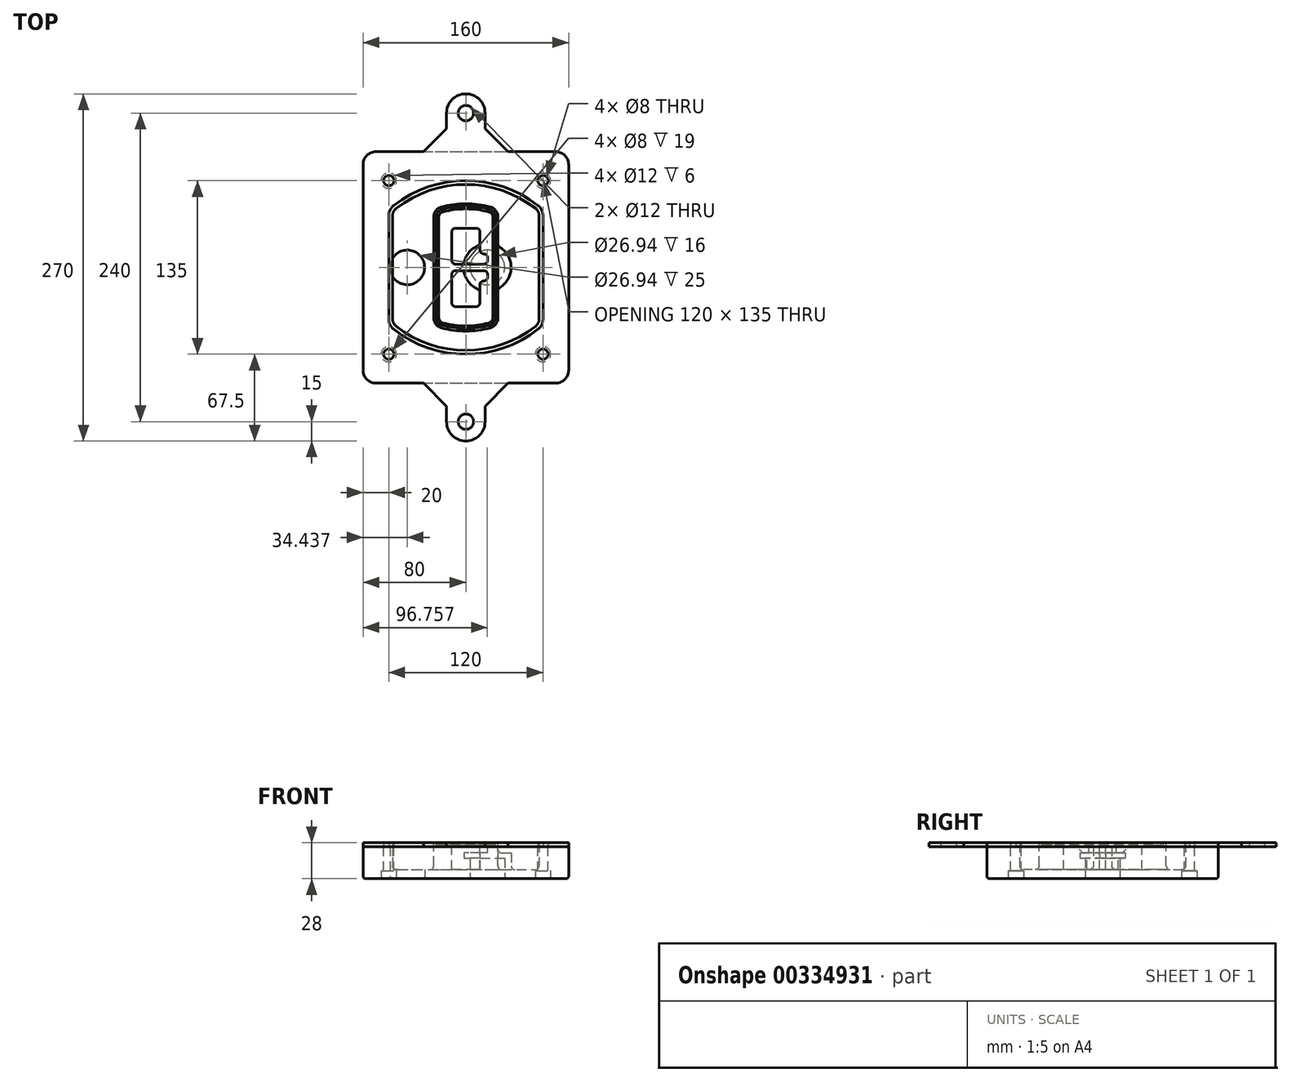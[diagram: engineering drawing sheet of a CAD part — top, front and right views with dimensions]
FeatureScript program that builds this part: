
annotation { "Feature Type Name" : "Feature", "Feature Type Description" : "" }
export const myFeature = defineFeature(function(context is Context, id is Id, definition is map)
    precondition{}
    {
        {
            var Q0;
            Q0=qCreatedBy(makeId("Top.planeOp"),FACE);
            var sketch = newSketch(context, id + "F0", { "sketchPlane" : qUnion([Q0])});
            skPoint(sketch, "E0.rect.middle", {"position": v(0, 0) * mm});
            skLineSegment(sketch, "E1.bottom", {"start": v(-70, -90) * mm, "end": v(70, -90) * mm});
            skLineSegment(sketch, "E1.top", {"start": v(-70, 90) * mm, "end": v(70, 90) * mm});
            skLineSegment(sketch, "E1.left", {"start": v(-80, -80) * mm, "end": v(-80, 80) * mm});
            skLineSegment(sketch, "E1.right", {"start": v(80, -80) * mm, "end": v(80, 80) * mm});
            skLineSegment(sketch, "E2", {"start": v(-80, 90) * mm, "end": v(80, -90) * mm, "construction": true});
            skLineSegment(sketch, "E3", {"start": v(80, 90) * mm, "end": v(-80, -90) * mm, "construction": true});
            skCircle(sketch, "E4", {"center": v(-60, 67.5) * mm, "radius": 4 * mm});
            skCircle(sketch, "E5", {"center": v(60, 67.5) * mm, "radius": 4 * mm});
            skCircle(sketch, "E6", {"center": v(60, -67.5) * mm, "radius": 4 * mm});
            skCircle(sketch, "E7", {"center": v(-60, -67.5) * mm, "radius": 4 * mm});
            skLineSegment(sketch, "E8", {"start": v(-60, 67.5) * mm, "end": v(60, 67.5) * mm, "construction": true});
            skLineSegment(sketch, "E9", {"start": v(60, 67.5) * mm, "end": v(60, -67.5) * mm, "construction": true});
            skLineSegment(sketch, "E10", {"start": v(60, -67.5) * mm, "end": v(-60, -67.5) * mm, "construction": true});
            skLineSegment(sketch, "E11", {"start": v(-60, -67.5) * mm, "end": v(-60, 67.5) * mm, "construction": true});
            skLineSegment(sketch, "E12", {"start": v(-60, 40.3) * mm, "end": v(-60, -40.3) * mm});
            skLineSegment(sketch, "E13", {"start": v(60, 40.3) * mm, "end": v(60, -40.3) * mm});
            skArc(sketch, "E14", {"start": v(56.15, 48.18) * mm, "mid": v(0, 67.5) * mm, "end": v(-56.15, 48.18) * mm});
            skArc(sketch, "E15", {"start": v(-56.15, -48.18) * mm, "mid": v(0, -67.5) * mm, "end": v(56.15, -48.18) * mm});
            skLineSegment(sketch, "E16", {"start": v(-60, 0) * mm, "end": v(60, 0) * mm, "construction": true});
            skPoint(sketch, "E17.visualSharp", {"position": v(-60, -45) * mm});
            skArc(sketch, "E17.filletArc", {"start": v(-60, -40.3) * mm, "mid": v(-58.99, -44.68) * mm, "end": v(-56.15, -48.18) * mm});
            skPoint(sketch, "E18.visualSharp", {"position": v(-60, 45) * mm});
            skArc(sketch, "E18.filletArc", {"start": v(-56.15, 48.18) * mm, "mid": v(-58.99, 44.68) * mm, "end": v(-60, 40.3) * mm});
            skPoint(sketch, "E19.visualSharp", {"position": v(60, 45) * mm});
            skArc(sketch, "E19.filletArc", {"start": v(60, 40.3) * mm, "mid": v(58.99, 44.68) * mm, "end": v(56.15, 48.18) * mm});
            skPoint(sketch, "E20.visualSharp", {"position": v(60, -45) * mm});
            skArc(sketch, "E20.filletArc", {"start": v(56.15, -48.18) * mm, "mid": v(58.99, -44.68) * mm, "end": v(60, -40.3) * mm});
            skPoint(sketch, "E21.visualSharp", {"position": v(-80, 90) * mm});
            skArc(sketch, "E21.filletArc", {"start": v(-70, 90) * mm, "mid": v(-77.07, 87.07) * mm, "end": v(-80, 80) * mm});
            skPoint(sketch, "E22.visualSharp", {"position": v(80, 90) * mm});
            skArc(sketch, "E22.filletArc", {"start": v(80, 80) * mm, "mid": v(77.07, 87.07) * mm, "end": v(70, 90) * mm});
            skPoint(sketch, "E23.visualSharp", {"position": v(80, -90) * mm});
            skArc(sketch, "E23.filletArc", {"start": v(70, -90) * mm, "mid": v(77.07, -87.07) * mm, "end": v(80, -80) * mm});
            skPoint(sketch, "E24.visualSharp", {"position": v(-80, -90) * mm});
            skArc(sketch, "E24.filletArc", {"start": v(-80, -80) * mm, "mid": v(-77.07, -87.07) * mm, "end": v(-70, -90) * mm});
            skArc(sketch, "E25.0", {"start": v(57, 40.3) * mm, "mid": v(56.3, 43.36) * mm, "end": v(54.3, 45.81) * mm});
            skLineSegment(sketch, "E25.1", {"start": v(57, 40.3) * mm, "end": v(57, -40.3) * mm});
            skArc(sketch, "E25.2", {"start": v(54.3, -45.81) * mm, "mid": v(56.3, -43.36) * mm, "end": v(57, -40.3) * mm});
            skArc(sketch, "E25.3", {"start": v(-54.3, -45.81) * mm, "mid": v(0, -64.5) * mm, "end": v(54.3, -45.81) * mm});
            skArc(sketch, "E25.4", {"start": v(-57, -40.3) * mm, "mid": v(-56.3, -43.36) * mm, "end": v(-54.3, -45.81) * mm});
            skArc(sketch, "E25.5", {"start": v(54.3, 45.81) * mm, "mid": v(0, 64.5) * mm, "end": v(-54.3, 45.81) * mm});
            skLineSegment(sketch, "E25.6", {"start": v(-57, 40.3) * mm, "end": v(-57, -40.3) * mm});
            skArc(sketch, "E25.7", {"start": v(-54.3, 45.81) * mm, "mid": v(-56.3, 43.36) * mm, "end": v(-57, 40.3) * mm});
            skArc(sketch, "E26.0", {"start": v(-58.62, 51.33) * mm, "mid": v(-62.58, 46.43) * mm, "end": v(-64, 40.3) * mm});
            skArc(sketch, "E26.1", {"start": v(58.62, 51.33) * mm, "mid": v(0, 71.5) * mm, "end": v(-58.62, 51.33) * mm});
            skArc(sketch, "E26.2", {"start": v(64, 40.3) * mm, "mid": v(62.58, 46.43) * mm, "end": v(58.62, 51.33) * mm});
            skLineSegment(sketch, "E26.3", {"start": v(64, 40.3) * mm, "end": v(64, -40.3) * mm});
            skArc(sketch, "E26.4", {"start": v(58.62, -51.33) * mm, "mid": v(62.58, -46.43) * mm, "end": v(64, -40.3) * mm});
            skLineSegment(sketch, "E26.5", {"start": v(-64, 40.3) * mm, "end": v(-64, -40.3) * mm});
            skArc(sketch, "E26.6", {"start": v(-58.62, -51.33) * mm, "mid": v(0, -71.5) * mm, "end": v(58.62, -51.33) * mm});
            skArc(sketch, "E26.7", {"start": v(-64, -40.3) * mm, "mid": v(-62.58, -46.43) * mm, "end": v(-58.62, -51.33) * mm});
            skSolve(sketch);
        }
        {
            var Q0;
            Q0=makeQuery(id+"F0.imprint","IMPRINT",FACE,{"disambiguationData":[TD([[makeQuery(id+"F0.imprint","IMPRINT",EDGE,{"derivedFrom":sQuery(id+"F0.wireOp",EDGE,"E1.bottom")}),1.0]])]});
            var Q1;
            Q1=makeQuery(id+"F0.imprint","IMPRINT",FACE,{"disambiguationData":[TD([[makeQuery(id+"F0.imprint","IMPRINT",EDGE,{"derivedFrom":sQuery(id+"F0.wireOp",EDGE,"E12")}),1.0]])]});
            var Q2;
            Q2=makeQuery(id+"F0.imprint","IMPRINT",FACE,{"disambiguationData":[TD([[makeQuery(id+"F0.imprint","IMPRINT",EDGE,{"derivedFrom":sQuery(id+"F0.wireOp",EDGE,"E25.0")}),1.0]])]});
            var Q3;
            Q3=makeQuery(id+"F0.imprint","IMPRINT",FACE,{"disambiguationData":[TD([[makeQuery(id+"F0.imprint","IMPRINT",EDGE,{"derivedFrom":sQuery(id+"F0.wireOp",EDGE,"E12")}),-1.0]])]});
            extrude(context, id + "F1", {"entities" : qUnion([Q0, Q1, Q2, Q3]), "oppositeDirection" : true, "depth" : 25 * mm});
        }
        {
            var Q0;
            Q0=makeQuery(id+"F0.imprint","IMPRINT",FACE,{"disambiguationData":[TD([[makeQuery(id+"F0.imprint","IMPRINT",EDGE,{"derivedFrom":sQuery(id+"F0.wireOp",EDGE,"E12")}),1.0]])]});
            extrude(context, id + "F2", {"entities" : qUnion([Q0]), "operationType" : NewBodyOperationType.ADD, "depth" : 3 * mm});
        }
        {
            var Q0;
            Q0=makeQuery(id+"F0.imprint","IMPRINT",FACE,{"disambiguationData":[TD([[makeQuery(id+"F0.imprint","IMPRINT",EDGE,{"derivedFrom":sQuery(id+"F0.wireOp",EDGE,"E25.0")}),1.0]])]});
            extrude(context, id + "F3", {"entities" : qUnion([Q0]), "operationType" : NewBodyOperationType.REMOVE, "oppositeDirection" : true, "depth" : 18 * mm});
        }
        {
            var Q0;
            Q0=makeQuery(id+"F2.opExtrude","CAP_FACE",FACE,{"disambiguationData":[OSD([sQuery(id+"F0.wireOp",EDGE,"E12"),sQuery(id+"F0.wireOp",EDGE,"E13"),sQuery(id+"F0.wireOp",EDGE,"E14"),sQuery(id+"F0.wireOp",EDGE,"E15"),sQuery(id+"F0.wireOp",EDGE,"E17.filletArc"),sQuery(id+"F0.wireOp",EDGE,"E18.filletArc"),sQuery(id+"F0.wireOp",EDGE,"E19.filletArc"),sQuery(id+"F0.wireOp",EDGE,"E20.filletArc"),sQuery(id+"F0.wireOp",EDGE,"E25.0"),sQuery(id+"F0.wireOp",EDGE,"E25.1"),sQuery(id+"F0.wireOp",EDGE,"E25.2"),sQuery(id+"F0.wireOp",EDGE,"E25.3"),sQuery(id+"F0.wireOp",EDGE,"E25.4"),sQuery(id+"F0.wireOp",EDGE,"E25.5"),sQuery(id+"F0.wireOp",EDGE,"E25.6"),sQuery(id+"F0.wireOp",EDGE,"E25.7")])],"isStart":false});
            var sketch = newSketch(context, id + "F4", { "sketchPlane" : qUnion([Q0])});
            skArc(sketch, "E27.0", {"start": v(-19.08, -46.97) * mm, "mid": v(0, -49.5) * mm, "end": v(19.08, -46.97) * mm});
            skArc(sketch, "E28.0", {"start": v(19.08, 46.97) * mm, "mid": v(0, 49.5) * mm, "end": v(-19.08, 46.97) * mm});
            skLineSegment(sketch, "E29", {"start": v(-25, 39.25) * mm, "end": v(-25, -39.25) * mm});
            skLineSegment(sketch, "E30", {"start": v(25, 39.25) * mm, "end": v(25, -39.25) * mm});
            skLineSegment(sketch, "E31", {"start": v(-25, 45.1) * mm, "end": v(25, 45.1) * mm, "construction": true});
            skLineSegment(sketch, "E32", {"start": v(-25, -45.1) * mm, "end": v(25, -45.1) * mm, "construction": true});
            skPoint(sketch, "E33.visualSharp", {"position": v(-25, 45.1) * mm});
            skArc(sketch, "E33.filletArc", {"start": v(-19.08, 46.97) * mm, "mid": v(-23.35, 44.11) * mm, "end": v(-25, 39.25) * mm});
            skPoint(sketch, "E34.visualSharp", {"position": v(25, 45.1) * mm});
            skArc(sketch, "E34.filletArc", {"start": v(25, 39.25) * mm, "mid": v(23.35, 44.11) * mm, "end": v(19.08, 46.97) * mm});
            skPoint(sketch, "E35.visualSharp", {"position": v(25, -45.1) * mm});
            skArc(sketch, "E35.filletArc", {"start": v(19.08, -46.97) * mm, "mid": v(23.35, -44.11) * mm, "end": v(25, -39.25) * mm});
            skPoint(sketch, "E36.visualSharp", {"position": v(-25, -45.1) * mm});
            skArc(sketch, "E36.filletArc", {"start": v(-25, -39.25) * mm, "mid": v(-23.35, -44.11) * mm, "end": v(-19.08, -46.97) * mm});
            skArc(sketch, "E37.0", {"start": v(54.3, 45.81) * mm, "mid": v(0, 64.5) * mm, "end": v(-54.3, 45.81) * mm});
            skArc(sketch, "E37.1", {"start": v(-54.3, 45.81) * mm, "mid": v(-56.3, 43.36) * mm, "end": v(-57, 40.3) * mm});
            skLineSegment(sketch, "E37.2", {"start": v(-57, 40.3) * mm, "end": v(-57, -40.3) * mm});
            skArc(sketch, "E37.3", {"start": v(-57, -40.3) * mm, "mid": v(-56.3, -43.36) * mm, "end": v(-54.3, -45.81) * mm});
            skArc(sketch, "E37.4", {"start": v(-54.3, -45.81) * mm, "mid": v(0, -64.5) * mm, "end": v(54.3, -45.81) * mm});
            skArc(sketch, "E37.5", {"start": v(54.3, -45.81) * mm, "mid": v(56.3, -43.36) * mm, "end": v(57, -40.3) * mm});
            skLineSegment(sketch, "E37.6", {"start": v(57, 40.3) * mm, "end": v(57, -40.3) * mm});
            skArc(sketch, "E37.7", {"start": v(57, 40.3) * mm, "mid": v(56.3, 43.36) * mm, "end": v(54.3, 45.81) * mm});
            skLineSegment(sketch, "E38.0", {"start": v(23, 39.25) * mm, "end": v(23, -39.25) * mm});
            skArc(sketch, "E38.1", {"start": v(18.56, -45.04) * mm, "mid": v(21.76, -42.9) * mm, "end": v(23, -39.25) * mm});
            skArc(sketch, "E38.2", {"start": v(-18.56, -45.04) * mm, "mid": v(0, -47.5) * mm, "end": v(18.56, -45.04) * mm});
            skArc(sketch, "E38.3", {"start": v(-23, -39.25) * mm, "mid": v(-21.76, -42.9) * mm, "end": v(-18.56, -45.04) * mm});
            skLineSegment(sketch, "E38.4", {"start": v(-23, 39.25) * mm, "end": v(-23, -39.25) * mm});
            skArc(sketch, "E38.5", {"start": v(23, 39.25) * mm, "mid": v(21.76, 42.9) * mm, "end": v(18.56, 45.04) * mm});
            skArc(sketch, "E38.6", {"start": v(-18.56, 45.04) * mm, "mid": v(-21.76, 42.9) * mm, "end": v(-23, 39.25) * mm});
            skArc(sketch, "E38.7", {"start": v(18.56, 45.04) * mm, "mid": v(0, 47.5) * mm, "end": v(-18.56, 45.04) * mm});
            skArc(sketch, "E39.0", {"start": v(21, 39.25) * mm, "mid": v(20.18, 41.68) * mm, "end": v(18.04, 43.1) * mm});
            skLineSegment(sketch, "E39.1", {"start": v(21, 39.25) * mm, "end": v(21, -39.25) * mm});
            skArc(sketch, "E39.2", {"start": v(18.04, -43.1) * mm, "mid": v(20.18, -41.68) * mm, "end": v(21, -39.25) * mm});
            skArc(sketch, "E39.3", {"start": v(-18.04, -43.1) * mm, "mid": v(0, -45.5) * mm, "end": v(18.04, -43.1) * mm});
            skArc(sketch, "E39.4", {"start": v(-21, -39.25) * mm, "mid": v(-20.18, -41.68) * mm, "end": v(-18.04, -43.1) * mm});
            skArc(sketch, "E39.5", {"start": v(18.04, 43.1) * mm, "mid": v(0, 45.5) * mm, "end": v(-18.04, 43.1) * mm});
            skLineSegment(sketch, "E39.6", {"start": v(-21, 39.25) * mm, "end": v(-21, -39.25) * mm});
            skArc(sketch, "E39.7", {"start": v(-18.04, 43.1) * mm, "mid": v(-20.18, 41.68) * mm, "end": v(-21, 39.25) * mm});
            skLineSegment(sketch, "E40", {"start": v(-25, 0) * mm, "end": v(25, 0) * mm, "construction": true});
            skLineSegment(sketch, "E41", {"start": v(-11, 5.5) * mm, "end": v(-11, 27.5) * mm});
            skLineSegment(sketch, "E42", {"start": v(-8, 30.5) * mm, "end": v(8, 30.5) * mm});
            skLineSegment(sketch, "E43", {"start": v(11, 27.5) * mm, "end": v(11, 13.5) * mm});
            skLineSegment(sketch, "E44", {"start": v(14, 10.5) * mm, "end": v(14, 10.5) * mm});
            skLineSegment(sketch, "E45", {"start": v(17, 7.5) * mm, "end": v(17, 5.5) * mm});
            skLineSegment(sketch, "E46", {"start": v(14, 2.5) * mm, "end": v(-8, 2.5) * mm});
            skPoint(sketch, "E47.visualSharp", {"position": v(-11, 30.5) * mm});
            skArc(sketch, "E47.filletArc", {"start": v(-8, 30.5) * mm, "mid": v(-10.12, 29.62) * mm, "end": v(-11, 27.5) * mm});
            skPoint(sketch, "E48.visualSharp", {"position": v(11, 30.5) * mm});
            skArc(sketch, "E48.filletArc", {"start": v(11, 27.5) * mm, "mid": v(10.12, 29.62) * mm, "end": v(8, 30.5) * mm});
            skPoint(sketch, "E49.visualSharp", {"position": v(11, 10.5) * mm});
            skArc(sketch, "E49.filletArc", {"start": v(11, 13.5) * mm, "mid": v(11.88, 11.38) * mm, "end": v(14, 10.5) * mm});
            skPoint(sketch, "E50.visualSharp", {"position": v(17, 10.5) * mm});
            skArc(sketch, "E50.filletArc", {"start": v(17, 7.5) * mm, "mid": v(16.12, 9.62) * mm, "end": v(14, 10.5) * mm});
            skPoint(sketch, "E51.visualSharp", {"position": v(17, 2.5) * mm});
            skArc(sketch, "E51.filletArc", {"start": v(14, 2.5) * mm, "mid": v(16.12, 3.38) * mm, "end": v(17, 5.5) * mm});
            skPoint(sketch, "E52.visualSharp", {"position": v(-11, 2.5) * mm});
            skArc(sketch, "E52.filletArc", {"start": v(-11, 5.5) * mm, "mid": v(-10.12, 3.38) * mm, "end": v(-8, 2.5) * mm});
            skLineSegment(sketch, "E53.0.MirrorCS", {"start": v(14, -2.5) * mm, "end": v(-8, -2.5) * mm});
            skArc(sketch, "E54.0.MirrorCS", {"start": v(-11, -5.5) * mm, "mid": v(-10.12, -3.38) * mm, "end": v(-8, -2.5) * mm});
            skLineSegment(sketch, "E55.0.MirrorCS", {"start": v(-11, -5.5) * mm, "end": v(-11, -27.5) * mm});
            skArc(sketch, "E56.0.MirrorCS", {"start": v(-8, -30.5) * mm, "mid": v(-10.12, -29.62) * mm, "end": v(-11, -27.5) * mm});
            skLineSegment(sketch, "E57.0.MirrorCS", {"start": v(-8, -30.5) * mm, "end": v(8, -30.5) * mm});
            skArc(sketch, "E58.0.MirrorCS", {"start": v(11, -27.5) * mm, "mid": v(10.12, -29.62) * mm, "end": v(8, -30.5) * mm});
            skLineSegment(sketch, "E59.0.MirrorCS", {"start": v(11, -27.5) * mm, "end": v(11, -13.5) * mm});
            skArc(sketch, "E60.0.MirrorCS", {"start": v(11, -13.5) * mm, "mid": v(11.88, -11.38) * mm, "end": v(14, -10.5) * mm});
            skArc(sketch, "E61.0.MirrorCS", {"start": v(17, -7.5) * mm, "mid": v(16.12, -9.62) * mm, "end": v(14, -10.5) * mm});
            skLineSegment(sketch, "E62.0.MirrorCS", {"start": v(17, -7.5) * mm, "end": v(17, -5.5) * mm});
            skArc(sketch, "E63.0.MirrorCS", {"start": v(14, -2.5) * mm, "mid": v(16.12, -3.38) * mm, "end": v(17, -5.5) * mm});
            skSolve(sketch);
        }
        {
            var Q0;
            Q0=makeQuery(id+"F4.imprint","IMPRINT",FACE,{"disambiguationData":[TD([[makeQuery(id+"F4.imprint","IMPRINT",EDGE,{"derivedFrom":sQuery(id+"F4.wireOp",EDGE,"E27.0")}),1.0]])]});
            var Q1;
            Q1=makeQuery(id+"F4.imprint","IMPRINT",FACE,{"disambiguationData":[TD([[makeQuery(id+"F4.imprint","IMPRINT",EDGE,{"derivedFrom":sQuery(id+"F4.wireOp",EDGE,"E38.0")}),-1.0]])]});
            var Q2;
            Q2=makeQuery(id+"F4.imprint","IMPRINT",FACE,{"disambiguationData":[TD([[makeQuery(id+"F4.imprint","IMPRINT",EDGE,{"derivedFrom":sQuery(id+"F4.wireOp",EDGE,"E39.0")}),1.0]])]});
            extrude(context, id + "F5", {"entities" : qUnion([Q0, Q1, Q2]), "operationType" : NewBodyOperationType.ADD, "endBound" : BoundingType.UP_TO_NEXT, "oppositeDirection" : true, "depth" : 25 * mm});
        }
        {
            var Q0;
            Q0=makeQuery(id+"F4.imprint","IMPRINT",FACE,{"disambiguationData":[TD([[makeQuery(id+"F4.imprint","IMPRINT",EDGE,{"derivedFrom":sQuery(id+"F4.wireOp",EDGE,"E38.0")}),-1.0]])]});
            extrude(context, id + "F6", {"entities" : qUnion([Q0]), "operationType" : NewBodyOperationType.REMOVE, "oppositeDirection" : true, "depth" : 2 * mm});
        }
        {
            var Q0;
            Q0=makeQuery(id+"F1.opExtrude","CAP_FACE",FACE,{"disambiguationData":[OSD([sQuery(id+"F0.wireOp",EDGE,"E1.bottom"),sQuery(id+"F0.wireOp",EDGE,"E1.top"),sQuery(id+"F0.wireOp",EDGE,"E1.left"),sQuery(id+"F0.wireOp",EDGE,"E1.right"),sQuery(id+"F0.wireOp",EDGE,"E4"),sQuery(id+"F0.wireOp",EDGE,"E5"),sQuery(id+"F0.wireOp",EDGE,"E6"),sQuery(id+"F0.wireOp",EDGE,"E7"),sQuery(id+"F0.wireOp",EDGE,"E21.filletArc"),sQuery(id+"F0.wireOp",EDGE,"E22.filletArc"),sQuery(id+"F0.wireOp",EDGE,"E23.filletArc"),sQuery(id+"F0.wireOp",EDGE,"E24.filletArc")])],"isStart":false});
            var sketch = newSketch(context, id + "F7", { "sketchPlane" : qUnion([Q0])});
            skCircle(sketch, "E64", {"center": v(16.76, 0) * mm, "radius": 13.47 * mm});
            skCircle(sketch, "E65", {"center": v(-45.56, 0) * mm, "radius": 13.47 * mm});
            skLineSegment(sketch, "E66", {"start": v(80, 0) * mm, "end": v(-80, 0) * mm});
            skCircle(sketch, "E67", {"center": v(16.76, 0) * mm, "radius": 18.47 * mm});
            skCircle(sketch, "E68", {"center": v(60, -67.5) * mm, "radius": 6 * mm});
            skCircle(sketch, "E69", {"center": v(-60, -67.5) * mm, "radius": 6 * mm});
            skCircle(sketch, "E70", {"center": v(-60, 67.5) * mm, "radius": 6 * mm});
            skCircle(sketch, "E71", {"center": v(60, 67.5) * mm, "radius": 6 * mm});
            skSolve(sketch);
        }
        {
            var Q0;
            {var subQ1=sQuery(id+"F7.wireOp",EDGE,"E66");var subQ4=sQuery(id+"F7.wireOp",EDGE,"E64");var subQ6=makeQuery(id+"F7.imprint","INTERSECT",VERTEX,{"disambiguationData":[OD(0.0)],"derivedFrom":[subQ4,subQ1]});Q0=makeQuery(id+"F7.imprint","IMPRINT",FACE,{"disambiguationData":[TD([[makeQuery(id+"F7.imprint","IMPRINT",EDGE,{"disambiguationData":[TD([[subQ6,-1.0]])],"derivedFrom":subQ4}),-1.0]])]});}
            var Q1;
            {var subQ0=sQuery(id+"F7.wireOp",EDGE,"E66");var subQ1=sQuery(id+"F7.wireOp",EDGE,"E64");var subQ3=makeQuery(id+"F7.imprint","INTERSECT",VERTEX,{"disambiguationData":[OD(0.0)],"derivedFrom":[subQ1,subQ0]});Q1=makeQuery(id+"F7.imprint","IMPRINT",FACE,{"disambiguationData":[TD([[makeQuery(id+"F7.imprint","IMPRINT",EDGE,{"disambiguationData":[TD([[subQ3,-1.0]])],"derivedFrom":subQ1}),1.0]])]});}
            var Q2;
            {var subQ0=sQuery(id+"F7.wireOp",EDGE,"E66");var subQ1=sQuery(id+"F7.wireOp",EDGE,"E64");var subQ3=makeQuery(id+"F7.imprint","INTERSECT",VERTEX,{"disambiguationData":[OD(0.0)],"derivedFrom":[subQ1,subQ0]});Q2=makeQuery(id+"F7.imprint","IMPRINT",FACE,{"disambiguationData":[TD([[makeQuery(id+"F7.imprint","IMPRINT",EDGE,{"disambiguationData":[TD([[subQ3,1.0]])],"derivedFrom":subQ1}),1.0]])]});}
            var Q3;
            {var subQ1=sQuery(id+"F7.wireOp",EDGE,"E66");var subQ4=sQuery(id+"F7.wireOp",EDGE,"E64");var subQ6=makeQuery(id+"F7.imprint","INTERSECT",VERTEX,{"disambiguationData":[OD(0.0)],"derivedFrom":[subQ4,subQ1]});Q3=makeQuery(id+"F7.imprint","IMPRINT",FACE,{"disambiguationData":[TD([[makeQuery(id+"F7.imprint","IMPRINT",EDGE,{"disambiguationData":[TD([[subQ6,1.0]])],"derivedFrom":subQ4}),-1.0]])]});}
            extrude(context, id + "F8", {"entities" : qUnion([Q0, Q1, Q2, Q3]), "operationType" : NewBodyOperationType.ADD, "oppositeDirection" : true, "depth" : 20 * mm});
        }
        {
            var Q0;
            {var subQ0=sQuery(id+"F7.wireOp",EDGE,"E66");var subQ1=sQuery(id+"F7.wireOp",EDGE,"E64");var subQ3=makeQuery(id+"F7.imprint","INTERSECT",VERTEX,{"disambiguationData":[OD(0.0)],"derivedFrom":[subQ1,subQ0]});Q0=makeQuery(id+"F7.imprint","IMPRINT",FACE,{"disambiguationData":[TD([[makeQuery(id+"F7.imprint","IMPRINT",EDGE,{"disambiguationData":[TD([[subQ3,-1.0]])],"derivedFrom":subQ1}),1.0]])]});}
            var Q1;
            {var subQ0=sQuery(id+"F7.wireOp",EDGE,"E66");var subQ1=sQuery(id+"F7.wireOp",EDGE,"E64");var subQ3=makeQuery(id+"F7.imprint","INTERSECT",VERTEX,{"disambiguationData":[OD(0.0)],"derivedFrom":[subQ1,subQ0]});Q1=makeQuery(id+"F7.imprint","IMPRINT",FACE,{"disambiguationData":[TD([[makeQuery(id+"F7.imprint","IMPRINT",EDGE,{"disambiguationData":[TD([[subQ3,1.0]])],"derivedFrom":subQ1}),1.0]])]});}
            extrude(context, id + "F9", {"entities" : qUnion([Q0, Q1]), "operationType" : NewBodyOperationType.REMOVE, "oppositeDirection" : true, "depth" : 16 * mm});
        }
        {
            var Q0;
            {var subQ0=sQuery(id+"F7.wireOp",EDGE,"E66");var subQ1=sQuery(id+"F7.wireOp",EDGE,"E65");var subQ3=makeQuery(id+"F7.imprint","INTERSECT",VERTEX,{"disambiguationData":[OD(0.0)],"derivedFrom":[subQ1,subQ0]});Q0=makeQuery(id+"F7.imprint","IMPRINT",FACE,{"disambiguationData":[TD([[makeQuery(id+"F7.imprint","IMPRINT",EDGE,{"disambiguationData":[TD([[subQ3,-1.0]])],"derivedFrom":subQ1}),1.0]])]});}
            var Q1;
            {var subQ0=sQuery(id+"F7.wireOp",EDGE,"E66");var subQ1=sQuery(id+"F7.wireOp",EDGE,"E65");var subQ3=makeQuery(id+"F7.imprint","INTERSECT",VERTEX,{"disambiguationData":[OD(0.0)],"derivedFrom":[subQ1,subQ0]});Q1=makeQuery(id+"F7.imprint","IMPRINT",FACE,{"disambiguationData":[TD([[makeQuery(id+"F7.imprint","IMPRINT",EDGE,{"disambiguationData":[TD([[subQ3,1.0]])],"derivedFrom":subQ1}),1.0]])]});}
            extrude(context, id + "F10", {"entities" : qUnion([Q0, Q1]), "operationType" : NewBodyOperationType.REMOVE, "oppositeDirection" : true, "depth" : 25 * mm});
        }
        {
            var Q0;
            Q0=makeQuery(id+"F7.imprint","IMPRINT",FACE,{"disambiguationData":[TD([[makeQuery(id+"F7.imprint","IMPRINT",EDGE,{"derivedFrom":sQuery(id+"F7.wireOp",EDGE,"E68")}),1.0]])]});
            var Q1;
            Q1=makeQuery(id+"F7.imprint","IMPRINT",FACE,{"disambiguationData":[TD([[makeQuery(id+"F7.imprint","IMPRINT",EDGE,{"derivedFrom":makeQuery(id+"F1.opExtrude","CAP_EDGE",EDGE,{"disambiguationData":[OSD([sQuery(id+"F0.wireOp",EDGE,"E5")])],"isStart":false})}),-1.0]])]});
            var Q2;
            Q2=makeQuery(id+"F7.imprint","IMPRINT",FACE,{"disambiguationData":[TD([[makeQuery(id+"F7.imprint","IMPRINT",EDGE,{"derivedFrom":sQuery(id+"F7.wireOp",EDGE,"E69")}),1.0]])]});
            var Q3;
            Q3=makeQuery(id+"F7.imprint","IMPRINT",FACE,{"disambiguationData":[TD([[makeQuery(id+"F7.imprint","IMPRINT",EDGE,{"derivedFrom":makeQuery(id+"F1.opExtrude","CAP_EDGE",EDGE,{"disambiguationData":[OSD([sQuery(id+"F0.wireOp",EDGE,"E4")])],"isStart":false})}),-1.0]])]});
            var Q4;
            Q4=makeQuery(id+"F7.imprint","IMPRINT",FACE,{"disambiguationData":[TD([[makeQuery(id+"F7.imprint","IMPRINT",EDGE,{"derivedFrom":sQuery(id+"F7.wireOp",EDGE,"E70")}),1.0]])]});
            var Q5;
            Q5=makeQuery(id+"F7.imprint","IMPRINT",FACE,{"disambiguationData":[TD([[makeQuery(id+"F7.imprint","IMPRINT",EDGE,{"derivedFrom":makeQuery(id+"F1.opExtrude","CAP_EDGE",EDGE,{"disambiguationData":[OSD([sQuery(id+"F0.wireOp",EDGE,"E7")])],"isStart":false})}),-1.0]])]});
            var Q6;
            Q6=makeQuery(id+"F7.imprint","IMPRINT",FACE,{"disambiguationData":[TD([[makeQuery(id+"F7.imprint","IMPRINT",EDGE,{"derivedFrom":sQuery(id+"F7.wireOp",EDGE,"E71")}),1.0]])]});
            var Q7;
            Q7=makeQuery(id+"F7.imprint","IMPRINT",FACE,{"disambiguationData":[TD([[makeQuery(id+"F7.imprint","IMPRINT",EDGE,{"derivedFrom":makeQuery(id+"F1.opExtrude","CAP_EDGE",EDGE,{"disambiguationData":[OSD([sQuery(id+"F0.wireOp",EDGE,"E6")])],"isStart":false})}),-1.0]])]});
            extrude(context, id + "F11", {"entities" : qUnion([Q0, Q1, Q2, Q3, Q4, Q5, Q6, Q7]), "operationType" : NewBodyOperationType.REMOVE, "oppositeDirection" : true, "depth" : 6 * mm});
        }
        {
            var Q0;
            Q0=makeQuery(id+"F9.boolean.opBoolean","COPY",FACE,{"derivedFrom":makeQuery(id+"F9.opExtrude","CAP_FACE",FACE,{"disambiguationData":[OSD([sQuery(id+"F7.wireOp",EDGE,"E64")])],"isStart":false})});
            var sketch = newSketch(context, id + "F12", { "sketchPlane" : qUnion([Q0])});
            skArc(sketch, "E72.0", {"start": v(11, 17.55) * mm, "mid": v(2.57, 11.82) * mm, "end": v(-1.54, 2.5) * mm});
            skArc(sketch, "E72.1", {"start": v(-1.54, -2.5) * mm, "mid": v(2.57, -11.82) * mm, "end": v(11, -17.55) * mm});
            skLineSegment(sketch, "E73", {"start": v(-1.54, -2.5) * mm, "end": v(14, -2.5) * mm});
            skLineSegment(sketch, "E74.0", {"start": v(14, 2.5) * mm, "end": v(-1.54, 2.5) * mm});
            skArc(sketch, "E74.1", {"start": v(14, 2.5) * mm, "mid": v(16.12, 3.38) * mm, "end": v(17, 5.5) * mm});
            skLineSegment(sketch, "E74.2", {"start": v(17, 7.5) * mm, "end": v(17, 5.5) * mm});
            skArc(sketch, "E74.3", {"start": v(17, 7.5) * mm, "mid": v(16.12, 9.62) * mm, "end": v(14, 10.5) * mm});
            skArc(sketch, "E74.4", {"start": v(11, 13.5) * mm, "mid": v(11.88, 11.38) * mm, "end": v(14, 10.5) * mm});
            skLineSegment(sketch, "E74.5", {"start": v(11, 17.55) * mm, "end": v(11, 13.5) * mm});
            skLineSegment(sketch, "E74.7", {"start": v(14, -2.5) * mm, "end": v(-1.54, -2.5) * mm});
            skArc(sketch, "E74.8", {"start": v(14, -2.5) * mm, "mid": v(16.12, -3.38) * mm, "end": v(17, -5.5) * mm});
            skLineSegment(sketch, "E74.9", {"start": v(17, -7.5) * mm, "end": v(17, -5.5) * mm});
            skArc(sketch, "E74.10", {"start": v(17, -7.5) * mm, "mid": v(16.12, -9.62) * mm, "end": v(14, -10.5) * mm});
            skArc(sketch, "E74.11", {"start": v(11, -13.5) * mm, "mid": v(11.88, -11.38) * mm, "end": v(14, -10.5) * mm});
            skLineSegment(sketch, "E74.12", {"start": v(11, -17.55) * mm, "end": v(11, -13.5) * mm});
            skPoint(sketch, "E75.orphan", {"position": v(11, -27.5) * mm});
            skPoint(sketch, "E76.orphan", {"position": v(-8, -2.5) * mm});
            skPoint(sketch, "E77.orphan", {"position": v(-8, 2.5) * mm});
            skPoint(sketch, "E78.orphan", {"position": v(11, 27.5) * mm});
            skSolve(sketch);
        }
        {
            var Q0;
            {var subQ7=sQuery(id+"F12.wireOp",EDGE,"E72.0");var subQ14=sQuery(id+"F12.wireOp",EDGE,"E72.1");var subQ16=sQuery(id+"F12.wireOp",EDGE,"E74.1");var subQ18=sQuery(id+"F12.wireOp",EDGE,"E74.8");Q0=qUnion([makeQuery(id+"F12.imprint","IMPRINT",FACE,{"disambiguationData":[TD([[makeQuery(id+"F12.imprint","IMPRINT",EDGE,{"derivedFrom":subQ7}),1.0]])]}),makeQuery(id+"F12.imprint","IMPRINT",FACE,{"disambiguationData":[TD([[makeQuery(id+"F12.imprint","IMPRINT",EDGE,{"derivedFrom":subQ14}),1.0]])]}),makeQuery(id+"F12.imprint","IMPRINT",FACE,{"disambiguationData":[TD([[makeQuery(id+"F12.imprint","IMPRINT",EDGE,{"derivedFrom":subQ16}),1.0]])]}),makeQuery(id+"F12.imprint","IMPRINT",FACE,{"disambiguationData":[TD([[makeQuery(id+"F12.imprint","IMPRINT",EDGE,{"derivedFrom":subQ18}),-1.0]])]})]);}
            var Q1;
            Q1=makeQuery(id+"F5.boolean.opBoolean","SPLIT",FACE,{"disambiguationData":[TD([makeQuery(id+"F5.opExtrude","SWEPT_FACE",FACE,{"disambiguationData":[OSD([sQuery(id+"F4.wireOp",EDGE,"E41")])]})])],"derivedFrom":makeQuery(id+"F3.boolean.opBoolean","COPY",FACE,{"derivedFrom":makeQuery(id+"F3.opExtrude","CAP_FACE",FACE,{"disambiguationData":[OSD([sQuery(id+"F0.wireOp",EDGE,"E25.0"),sQuery(id+"F0.wireOp",EDGE,"E25.1"),sQuery(id+"F0.wireOp",EDGE,"E25.2"),sQuery(id+"F0.wireOp",EDGE,"E25.3"),sQuery(id+"F0.wireOp",EDGE,"E25.4"),sQuery(id+"F0.wireOp",EDGE,"E25.5"),sQuery(id+"F0.wireOp",EDGE,"E25.6"),sQuery(id+"F0.wireOp",EDGE,"E25.7")])],"isStart":false})})});
            extrude(context, id + "F13", {"entities" : qUnion([Q0]), "operationType" : NewBodyOperationType.REMOVE, "endBound" : BoundingType.UP_TO_SURFACE, "endBoundEntityFace" : qUnion([Q1]), "depth" : 25 * mm});
        }
        {
            var Q0;
            Q0=makeQuery(id+"F3.boolean.opBoolean","COPY",EDGE,{"derivedFrom":makeQuery(id+"F3.opExtrude","CAP_EDGE",EDGE,{"disambiguationData":[OSD([sQuery(id+"F0.wireOp",EDGE,"E25.6")])],"isStart":false})});
            var Q1;
            Q1=makeQuery(id+"F8.boolean.opBoolean","INTERSECT",EDGE,{"derivedFrom":[makeQuery(id+"F5.opExtrude","SWEPT_FACE",FACE,{"disambiguationData":[OSD([sQuery(id+"F4.wireOp",EDGE,"E30")])]}),makeQuery(id+"F8.opExtrude","CAP_FACE",FACE,{"disambiguationData":[OSD([sQuery(id+"F7.wireOp",EDGE,"E67")])],"isStart":false})]});
            var Q2;
            Q2=makeQuery(id+"F8.boolean.opBoolean","INTERSECT",EDGE,{"disambiguationData":[OD(1.0)],"derivedFrom":[makeQuery(id+"F5.opExtrude","SWEPT_FACE",FACE,{"disambiguationData":[OSD([sQuery(id+"F4.wireOp",EDGE,"E30")])]}),makeQuery(id+"F8.opExtrude","SWEPT_FACE",FACE,{"disambiguationData":[OSD([sQuery(id+"F7.wireOp",EDGE,"E67")])]})]});
            var Q3;
            {var subQ0=sQuery(id+"F4.wireOp",EDGE,"E30");Q3=makeQuery(id+"F8.boolean.opBoolean","SPLIT",EDGE,{"disambiguationData":[TD([makeQuery(id+"F5.opExtrude","SWEPT_FACE",FACE,{"disambiguationData":[OSD([sQuery(id+"F4.wireOp",EDGE,"E35.filletArc")])]})])],"derivedFrom":makeQuery(id+"F5.opExtrude","CAP_EDGE",EDGE,{"disambiguationData":[OSD([subQ0])],"isStart":false})});}
            var Q4;
            {var subQ0=sQuery(id+"F0.wireOp",EDGE,"E25.7");var subQ1=sQuery(id+"F0.wireOp",EDGE,"E25.1");var subQ2=sQuery(id+"F0.wireOp",EDGE,"E25.6");var subQ3=sQuery(id+"F0.wireOp",EDGE,"E25.5");var subQ4=sQuery(id+"F0.wireOp",EDGE,"E25.4");var subQ5=sQuery(id+"F0.wireOp",EDGE,"E25.0");var subQ6=sQuery(id+"F0.wireOp",EDGE,"E25.2");var subQ7=sQuery(id+"F0.wireOp",EDGE,"E25.3");Q4=makeQuery(id+"F8.boolean.opBoolean","INTERSECT",EDGE,{"derivedFrom":[makeQuery(id+"F5.boolean.opBoolean","SPLIT",FACE,{"disambiguationData":[TD([makeQuery(id+"F2.opExtrude","SWEPT_FACE",FACE,{"disambiguationData":[OSD([subQ5])]})])],"derivedFrom":makeQuery(id+"F3.boolean.opBoolean","COPY",FACE,{"derivedFrom":makeQuery(id+"F3.opExtrude","CAP_FACE",FACE,{"disambiguationData":[OSD([subQ5,subQ1,subQ6,subQ7,subQ4,subQ3,subQ2,subQ0])],"isStart":false})})}),makeQuery(id+"F8.opExtrude","SWEPT_FACE",FACE,{"disambiguationData":[OSD([sQuery(id+"F7.wireOp",EDGE,"E67")])]})]});}
            var Q5;
            Q5=makeQuery(id+"F8.boolean.opBoolean","INTERSECT",EDGE,{"disambiguationData":[OD(0.0)],"derivedFrom":[makeQuery(id+"F5.opExtrude","SWEPT_FACE",FACE,{"disambiguationData":[OSD([sQuery(id+"F4.wireOp",EDGE,"E30")])]}),makeQuery(id+"F8.opExtrude","SWEPT_FACE",FACE,{"disambiguationData":[OSD([sQuery(id+"F7.wireOp",EDGE,"E67")])]})]});
            fillet(context, id + "F14", {"entities" : qUnion([Q0, Q1, Q2, Q3, Q4, Q5]), "radius" : 3 * mm, "tangentPropagation" : true, "allowEdgeOverflow" : false});
        }
        {
            var Q0;
            Q0=makeQuery(id+"F1.opExtrude","CAP_EDGE",EDGE,{"disambiguationData":[OSD([sQuery(id+"F0.wireOp",EDGE,"E1.bottom")])],"isStart":false});
            fillet(context, id + "F15", {"entities" : qUnion([Q0]), "radius" : 2 * mm, "tangentPropagation" : true, "allowEdgeOverflow" : false});
        }
        {
            var Q0;
            {var subQ0=sQuery(id+"F0.wireOp",EDGE,"E21.filletArc");var subQ1=sQuery(id+"F0.wireOp",EDGE,"E7");var subQ2=sQuery(id+"F0.wireOp",EDGE,"E6");var subQ3=sQuery(id+"F0.wireOp",EDGE,"E5");var subQ4=sQuery(id+"F0.wireOp",EDGE,"E4");var subQ5=sQuery(id+"F0.wireOp",EDGE,"E22.filletArc");var subQ6=sQuery(id+"F0.wireOp",EDGE,"E1.bottom");var subQ7=sQuery(id+"F0.wireOp",EDGE,"E1.right");var subQ8=sQuery(id+"F0.wireOp",EDGE,"E1.top");var subQ9=sQuery(id+"F0.wireOp",EDGE,"E1.left");var subQ10=sQuery(id+"F0.wireOp",EDGE,"E23.filletArc");var subQ11=sQuery(id+"F0.wireOp",EDGE,"E24.filletArc");Q0=makeQuery(id+"F2.boolean.opBoolean","SPLIT",FACE,{"disambiguationData":[TD([makeQuery(id+"F1.opExtrude","SWEPT_FACE",FACE,{"disambiguationData":[OSD([subQ6])]})])],"derivedFrom":makeQuery(id+"F1.opExtrude","CAP_FACE",FACE,{"disambiguationData":[OSD([subQ6,subQ8,subQ9,subQ7,subQ4,subQ3,subQ2,subQ1,subQ0,subQ5,subQ10,subQ11])],"isStart":true})});}
            var sketch = newSketch(context, id + "F16", { "sketchPlane" : qUnion([Q0])});
            skCircle(sketch, "E79", {"center": v(0, 120) * mm, "radius": 6 * mm});
            skPoint(sketch, "E79.centerSnap0", {"position": v(0, 90) * mm});
            skLineSegment(sketch, "E80", {"start": v(-15.03, 120) * mm, "end": v(-15.03, 108) * mm});
            skLineSegment(sketch, "E81", {"start": v(-15.03, 108) * mm, "end": v(-33.03, 90) * mm});
            skLineSegment(sketch, "E82", {"start": v(14.97, 120) * mm, "end": v(14.97, 108) * mm});
            skLineSegment(sketch, "E83", {"start": v(14.97, 108) * mm, "end": v(32.97, 90) * mm});
            skArc(sketch, "E84", {"start": v(14.97, 120) * mm, "mid": v(-0.03, 135) * mm, "end": v(-15.03, 120) * mm});
            skLineSegment(sketch, "E85", {"start": v(-80, 0) * mm, "end": v(80, 0) * mm, "construction": true});
            skLineSegment(sketch, "E86.MirrorCS", {"start": v(14.97, -108) * mm, "end": v(32.97, -90) * mm});
            skLineSegment(sketch, "E87.MirrorCS", {"start": v(14.97, -120) * mm, "end": v(14.97, -108) * mm});
            skArc(sketch, "E88.MirrorCS", {"start": v(14.97, -120) * mm, "mid": v(-0.03, -135) * mm, "end": v(-15.03, -120) * mm});
            skLineSegment(sketch, "E89.MirrorCS", {"start": v(-15.03, -108) * mm, "end": v(-33.03, -90) * mm});
            skLineSegment(sketch, "E90.MirrorCS", {"start": v(-15.03, -120) * mm, "end": v(-15.03, -108) * mm});
            skCircle(sketch, "E91.MirrorC", {"center": v(0, -120) * mm, "radius": 6 * mm});
            skPoint(sketch, "E92.MirrorP", {"position": v(0, -90) * mm});
            skLineSegment(sketch, "E93", {"start": v(0, 120) * mm, "end": v(0, 90) * mm, "construction": true});
            skLineSegment(sketch, "E94", {"start": v(0, -120) * mm, "end": v(0, -90) * mm, "construction": true});
            skSolve(sketch);
        }
        {
            var Q0;
            Q0=makeQuery(id+"F16.imprint","IMPRINT",FACE,{"disambiguationData":[TD([[makeQuery(id+"F16.imprint","IMPRINT",EDGE,{"derivedFrom":sQuery(id+"F16.wireOp",EDGE,"E79")}),-1.0]])]});
            var Q1;
            {var subQ1=sQuery(id+"F16.wireOp",EDGE,"E86.MirrorCS");Q1=makeQuery(id+"F16.imprint","IMPRINT",FACE,{"disambiguationData":[TD([[makeQuery(id+"F16.imprint","IMPRINT",EDGE,{"derivedFrom":subQ1}),1.0]])]});}
            var Q2;
            Q2=makeQuery(id+"F16.imprint","IMPRINT",FACE,{"disambiguationData":[TD([[makeQuery(id+"F16.imprint","IMPRINT",EDGE,{"derivedFrom":makeQuery(id+"F1.opExtrude","CAP_EDGE",EDGE,{"disambiguationData":[OSD([sQuery(id+"F0.wireOp",EDGE,"E1.left")])],"isStart":true})}),-1.0]])]});
            var Q3;
            Q3=makeQuery(id+"F2.opExtrude","CAP_FACE",FACE,{"disambiguationData":[OSD([sQuery(id+"F0.wireOp",EDGE,"E12"),sQuery(id+"F0.wireOp",EDGE,"E13"),sQuery(id+"F0.wireOp",EDGE,"E14"),sQuery(id+"F0.wireOp",EDGE,"E15"),sQuery(id+"F0.wireOp",EDGE,"E17.filletArc"),sQuery(id+"F0.wireOp",EDGE,"E18.filletArc"),sQuery(id+"F0.wireOp",EDGE,"E19.filletArc"),sQuery(id+"F0.wireOp",EDGE,"E20.filletArc"),sQuery(id+"F0.wireOp",EDGE,"E25.0"),sQuery(id+"F0.wireOp",EDGE,"E25.1"),sQuery(id+"F0.wireOp",EDGE,"E25.2"),sQuery(id+"F0.wireOp",EDGE,"E25.3"),sQuery(id+"F0.wireOp",EDGE,"E25.4"),sQuery(id+"F0.wireOp",EDGE,"E25.5"),sQuery(id+"F0.wireOp",EDGE,"E25.6"),sQuery(id+"F0.wireOp",EDGE,"E25.7")])],"isStart":false});
            extrude(context, id + "F17", {"entities" : qUnion([Q0, Q1, Q2]), "endBound" : BoundingType.UP_TO_SURFACE, "endBoundEntityFace" : qUnion([Q3]), "depth" : 25 * mm});
        }
    });
